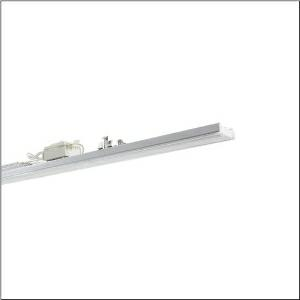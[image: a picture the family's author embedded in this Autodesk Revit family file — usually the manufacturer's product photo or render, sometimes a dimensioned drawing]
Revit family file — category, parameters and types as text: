
# Revit family: licross_r__11_recessed_ho_51tl1ede465s_4e4a
name_source: partatom
category: Lighting Fixtures
units: mm (PartAtom-declared; Revit-internal decimal feet)

## family parameters
Cut with Voids When Loaded = No
Host = Face
Light Source = No
Part Type = Normal
Room Calculation Point = No
Round Connector Dimension = Use Diameter
Shared = No

## types (1)
- --- (1 x LED, 6840 lm, 40.2 W, 4000K)
    Apparent Load = 40 VA
    CIE Flux Codes = 85 95 99 100 100
    Color Rendering = 80
    Color Temperature = 4000K
    Default Elevation = 1800 mm
    Description = Licross® 11 Recessed HO, luminaire insert, of sheet steel, coil coated, white, length: 750mm, width: 66mm, height: 67mm, LED rated luminous flux: 6.840lm, light colour: 840, control gear: DALI 2, with plug, 5-pole, with phase selection, mains connection: 220..240V, AC, 50/60Hz, rated input power: 40W, internal wiring halogen-free, primary light control with lens, of plastic, primary optical cover: cover, of PMMA, light emission: direct distribution, primary light characteristic: symmetric, protection rating (complete): IP40, insulation class (complete): insulation class I (protective earthing), certification: CE, ENEC, VDE, UKCA, protection symbol: D if used in an environment without relevant dust loads with corresponding accessories, impact resistance: IK06, permissible ambient temperature for indoor applications: -25..+30°C, corresponds to IFS (International Featured Standards) requirements for safety and quality in the food industry, reducing of maximum allowable ambient temperature of 5°C with ceiling mounting, LABS conformity tested according to VDMA 24364:2018-05, packaging unit: 1 piece
    Height = 58 mm
    Lamp = 1 x LED
    Lamp Light Flux = 6840 lm
    Lamp Power = 40.2 W
    Lamp count = 1
    Length = 750 mm
    Luminous efficacy = 170 lm/W
    Manufacturer = Siteco
    ModVariant = No
    Model = 51TL1EDE465S
    Mounting Place = Ceiling
    Mounting Type = Pendant
    Number of Poles = 1
    OnlyDefault = Yes
    Power Factor = 1
    Product Name = Licross® 11 Recessed HO
    Product group = luminaire insert | ceiling pendant
    ProductGroupID = 902
    Protection Class = Protection class I
    Protection Degree = IP 40
    RLX_Detail_Level = 1
    RLX_Emergency_Light_Flux = 0 lm
    RLX_Emergency_Type = 0
    RLX_Emergency_Type_DB = No
    RlxData = <blob elided: 29329 chars, md5=54fa5264>
    Socket = socket
    Standby Power = 0 W
    System Light Flux = 6840 lm
    System Power = 40 W
    Type Comments = factory setting: luminous flux: 100 % | dim-lin: 254 | 522 mA
    Type Image = l_1296930.jpg
    URL = http://relux.com
    VarID = @adj_117105
    Voltage = 0 V
    Weight = 0.00 kg
    Width = 66 mm

## geometry (parser evidence)
native form markers: Blend x4, Sweep x10
no freeform markers — native parametric forms only
